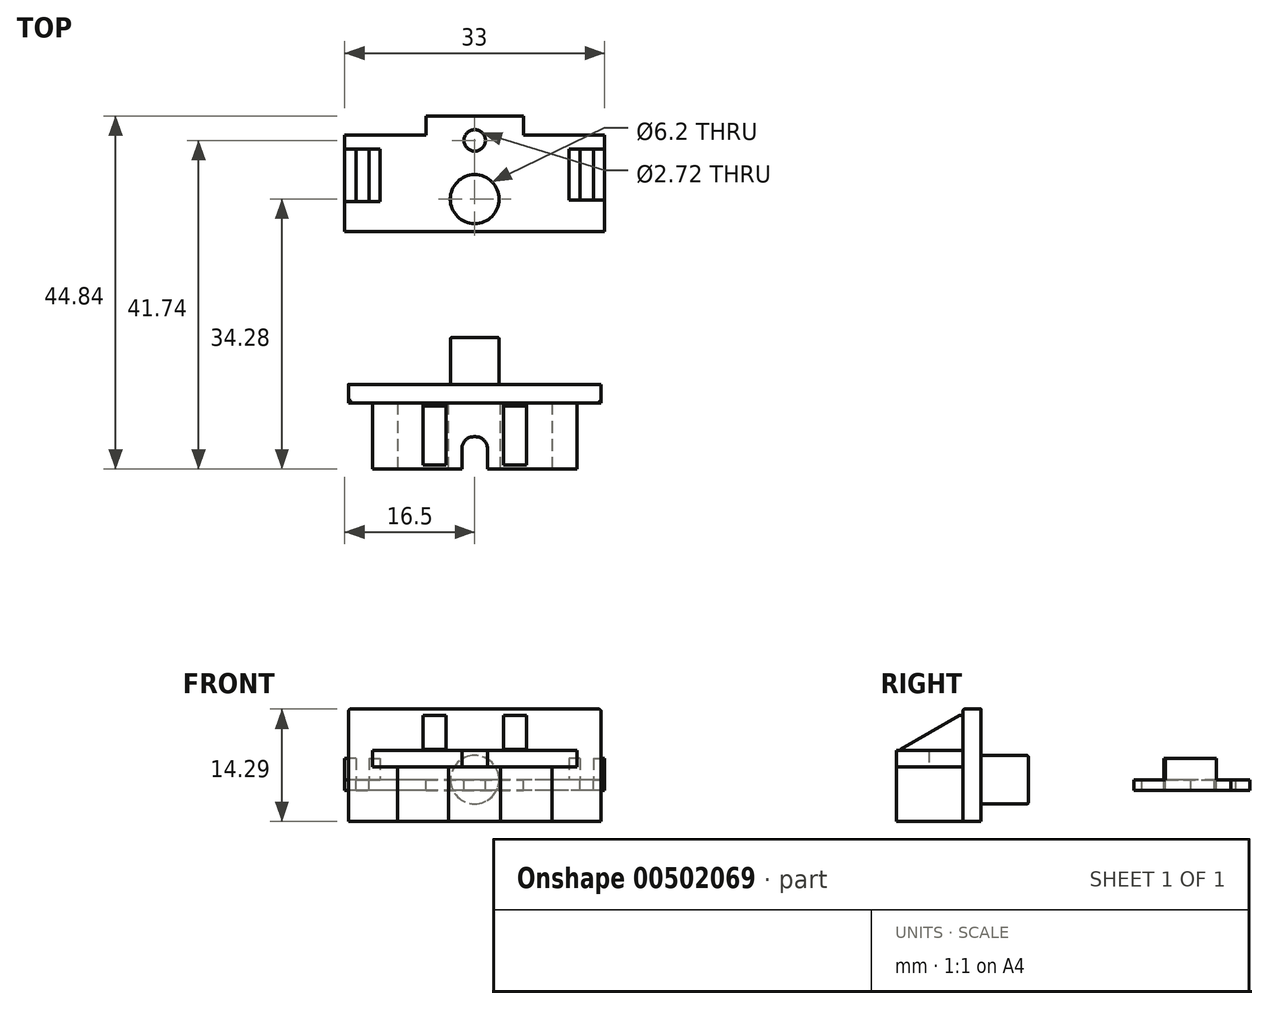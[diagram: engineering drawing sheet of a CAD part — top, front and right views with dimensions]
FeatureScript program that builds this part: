
annotation { "Feature Type Name" : "Feature", "Feature Type Description" : "" }
export const myFeature = defineFeature(function(context is Context, id is Id, definition is map)
    precondition{}
    {
        {
            var Q0;
            Q0=qCreatedBy(makeId("Top.planeOp"),FACE);
            var sketch = newSketch(context, id + "F0", { "sketchPlane" : qUnion([Q0])});
            skLineSegment(sketch, "E0.bottom", {"start": v(16.5, 6.15) * mm, "end": v(-16.5, 6.15) * mm});
            skLineSegment(sketch, "E0.top", {"start": v(16.5, -6.15) * mm, "end": v(-16.5, -6.15) * mm});
            skLineSegment(sketch, "E0.left", {"start": v(16.5, 6.15) * mm, "end": v(16.5, -6.15) * mm});
            skLineSegment(sketch, "E0.right", {"start": v(-16.5, 6.15) * mm, "end": v(-16.5, -6.15) * mm});
            skPoint(sketch, "E0.middle", {"position": v(0, 0) * mm});
            skCircle(sketch, "E1", {"center": v(0, -2) * mm, "radius": 3.1 * mm});
            skPoint(sketch, "E2.endSnap0", {"position": v(0, 6.15) * mm});
            skPoint(sketch, "E3", {"position": v(-6.2, 6.15) * mm});
            skPoint(sketch, "E4", {"position": v(6.2, 6.15) * mm});
            skLineSegment(sketch, "E5.bottom", {"start": v(-6.2, 6.15) * mm, "end": v(6.2, 6.15) * mm});
            skLineSegment(sketch, "E5.top", {"start": v(-6.2, 8.56) * mm, "end": v(6.2, 8.56) * mm});
            skLineSegment(sketch, "E5.left", {"start": v(-6.2, 6.15) * mm, "end": v(-6.2, 8.56) * mm});
            skLineSegment(sketch, "E5.right", {"start": v(6.2, 6.15) * mm, "end": v(6.2, 8.56) * mm});
            skCircle(sketch, "E6", {"center": v(0, 5.46) * mm, "radius": 1.36 * mm});
            skLineSegment(sketch, "E7", {"start": v(-15.1, 4.35) * mm, "end": v(-15.1, -2.31) * mm});
            skLineSegment(sketch, "E8", {"start": v(15.1, 4.35) * mm, "end": v(15.1, -2.15) * mm});
            skLineSegment(sketch, "E9", {"start": v(-13.4, -2.31) * mm, "end": v(-15.1, -2.31) * mm});
            skLineSegment(sketch, "E10", {"start": v(15.1, -2.15) * mm, "end": v(13.4, -2.15) * mm});
            skLineSegment(sketch, "E11", {"start": v(15.1, 4.35) * mm, "end": v(13.4, 4.35) * mm});
            skLineSegment(sketch, "E12", {"start": v(13.4, -2.15) * mm, "end": v(13.4, 4.35) * mm});
            skLineSegment(sketch, "E13", {"start": v(-13.4, 4.35) * mm, "end": v(-13.4, -2.3) * mm});
            skLineSegment(sketch, "E14", {"start": v(-15.1, 4.35) * mm, "end": v(-13.4, 4.35) * mm});
            skLineSegment(sketch, "E15", {"start": v(-15.1, 4.35) * mm, "end": v(-16.5, 4.35) * mm});
            skLineSegment(sketch, "E16", {"start": v(-15.1, -2.31) * mm, "end": v(-16.5, -2.31) * mm});
            skLineSegment(sketch, "E17.0", {"start": v(-12, 4.35) * mm, "end": v(-12, -2.3) * mm});
            skLineSegment(sketch, "E18", {"start": v(-13.4, 4.35) * mm, "end": v(-12, 4.35) * mm});
            skLineSegment(sketch, "E19", {"start": v(-13.4, -2.31) * mm, "end": v(-12, -2.3) * mm});
            skLineSegment(sketch, "E20", {"start": v(15.1, 4.35) * mm, "end": v(16.5, 4.35) * mm});
            skLineSegment(sketch, "E21", {"start": v(15.1, -2.15) * mm, "end": v(16.5, -2.15) * mm});
            skLineSegment(sketch, "E22.0", {"start": v(12, -2.15) * mm, "end": v(12, 4.35) * mm});
            skLineSegment(sketch, "E23", {"start": v(13.4, 4.35) * mm, "end": v(12, 4.35) * mm});
            skLineSegment(sketch, "E24", {"start": v(13.4, -2.15) * mm, "end": v(12, -2.15) * mm});
            skLineSegment(sketch, "E25.bottom", {"start": v(3.08, -25.55) * mm, "end": v(-3.07, -25.55) * mm});
            skLineSegment(sketch, "E25.top", {"start": v(3.08, -19.55) * mm, "end": v(-3.07, -19.55) * mm});
            skLineSegment(sketch, "E25.left", {"start": v(3.08, -25.55) * mm, "end": v(3.08, -19.55) * mm});
            skLineSegment(sketch, "E25.right", {"start": v(-3.07, -25.55) * mm, "end": v(-3.07, -19.55) * mm});
            skPoint(sketch, "E25.middle", {"position": v(0, -22.55) * mm});
            skLineSegment(sketch, "E26", {"start": v(0, -25.55) * mm, "end": v(16.03, -25.55) * mm});
            skLineSegment(sketch, "E27", {"start": v(0, -25.55) * mm, "end": v(-16.03, -25.55) * mm});
            skLineSegment(sketch, "E28.bottom", {"start": v(-16.03, -25.55) * mm, "end": v(16.03, -25.55) * mm});
            skLineSegment(sketch, "E28.top", {"start": v(-16.03, -27.88) * mm, "end": v(16.03, -27.88) * mm});
            skLineSegment(sketch, "E28.left", {"start": v(-16.03, -25.55) * mm, "end": v(-16.03, -27.88) * mm});
            skLineSegment(sketch, "E28.right", {"start": v(16.03, -25.55) * mm, "end": v(16.03, -27.88) * mm});
            skLineSegment(sketch, "E29.bottom", {"start": v(13, -27.88) * mm, "end": v(-13, -27.88) * mm});
            skLineSegment(sketch, "E29.top", {"start": v(13, -36.28) * mm, "end": v(-13, -36.28) * mm});
            skLineSegment(sketch, "E29.left", {"start": v(13, -27.88) * mm, "end": v(13, -36.28) * mm});
            skLineSegment(sketch, "E29.right", {"start": v(-13, -27.88) * mm, "end": v(-13, -36.28) * mm});
            skPoint(sketch, "E30", {"position": v(1.6, -36.28) * mm});
            skPoint(sketch, "E31", {"position": v(-1.61, -36.28) * mm});
            skPoint(sketch, "E32", {"position": v(0, -36.28) * mm});
            skLineSegment(sketch, "E33.bottom", {"start": v(-1.61, -36.28) * mm, "end": v(1.6, -36.28) * mm});
            skLineSegment(sketch, "E33.top", {"start": v(-1.61, -32.18) * mm, "end": v(1.6, -32.18) * mm});
            skLineSegment(sketch, "E33.left", {"start": v(-1.61, -36.28) * mm, "end": v(-1.61, -32.18) * mm});
            skLineSegment(sketch, "E33.right", {"start": v(1.6, -36.28) * mm, "end": v(1.6, -32.18) * mm});
            skLineSegment(sketch, "E34", {"start": v(-1.61, -32.18) * mm, "end": v(-3.31, -32.18) * mm});
            skLineSegment(sketch, "E35", {"start": v(1.6, -32.18) * mm, "end": v(3.3, -32.18) * mm});
            skLineSegment(sketch, "E36", {"start": v(-3.31, -36.28) * mm, "end": v(-3.31, -27.88) * mm});
            skLineSegment(sketch, "E37", {"start": v(3.3, -36.28) * mm, "end": v(3.3, -27.88) * mm});
            skLineSegment(sketch, "E38", {"start": v(-6.81, -27.88) * mm, "end": v(-6.8, -36.28) * mm});
            skLineSegment(sketch, "E39", {"start": v(6.8, -27.88) * mm, "end": v(6.81, -36.28) * mm});
            skLineSegment(sketch, "E40", {"start": v(-9.8, -27.88) * mm, "end": v(-9.8, -36.28) * mm});
            skLineSegment(sketch, "E41", {"start": v(9.8, -27.88) * mm, "end": v(9.8, -36.28) * mm});
            skLineSegment(sketch, "E42", {"start": v(0, -19.55) * mm, "end": v(0, -25.55) * mm});
            skSolve(sketch);
        }
        {
            var Q0;
            {var subQ10=sQuery(id+"F0.wireOp",EDGE,"E0.top");Q0=makeQuery(id+"F0.imprint","IMPRINT",FACE,{"disambiguationData":[TD([[makeQuery(id+"F0.imprint","IMPRINT",EDGE,{"derivedFrom":subQ10}),-1.0]])]});}
            var Q1;
            Q1=makeQuery(id+"F0.imprint","IMPRINT",FACE,{"disambiguationData":[TD([[makeQuery(id+"F0.imprint","IMPRINT",EDGE,{"derivedFrom":sQuery(id+"F0.wireOp",EDGE,"E7")}),-1.0]])]});
            var Q2;
            Q2=makeQuery(id+"F0.imprint","IMPRINT",FACE,{"disambiguationData":[TD([[makeQuery(id+"F0.imprint","IMPRINT",EDGE,{"derivedFrom":sQuery(id+"F0.wireOp",EDGE,"E12")}),1.0]])]});
            var Q3;
            Q3=makeQuery(id+"F0.imprint","IMPRINT",FACE,{"disambiguationData":[TD([[makeQuery(id+"F0.imprint","IMPRINT",EDGE,{"derivedFrom":sQuery(id+"F0.wireOp",EDGE,"E5.top")}),-1.0]])]});
            var Q4;
            Q4=makeQuery(id+"F0.imprint","IMPRINT",FACE,{"disambiguationData":[TD([[makeQuery(id+"F0.imprint","IMPRINT",EDGE,{"derivedFrom":sQuery(id+"F0.wireOp",EDGE,"E8")}),1.0]])]});
            var Q5;
            Q5=makeQuery(id+"F0.imprint","IMPRINT",FACE,{"disambiguationData":[TD([[makeQuery(id+"F0.imprint","IMPRINT",EDGE,{"derivedFrom":sQuery(id+"F0.wireOp",EDGE,"E13")}),1.0]])]});
            extrude(context, id + "F1", {"entities" : qUnion([Q0, Q1, Q2, Q3, Q4, Q5]), "oppositeDirection" : true, "depth" : 1.35 * mm});
        }
        {
            var Q0;
            Q0=makeQuery(id+"F0.imprint","IMPRINT",FACE,{"disambiguationData":[TD([[makeQuery(id+"F0.imprint","IMPRINT",EDGE,{"derivedFrom":sQuery(id+"F0.wireOp",EDGE,"E13")}),1.0]])]});
            var Q1;
            Q1=makeQuery(id+"F0.imprint","IMPRINT",FACE,{"disambiguationData":[TD([[makeQuery(id+"F0.imprint","IMPRINT",EDGE,{"derivedFrom":sQuery(id+"F0.wireOp",EDGE,"E12")}),1.0]])]});
            var Q2;
            Q2=makeQuery(id+"F0.imprint","IMPRINT",FACE,{"disambiguationData":[TD([[makeQuery(id+"F0.imprint","IMPRINT",EDGE,{"derivedFrom":sQuery(id+"F0.wireOp",EDGE,"E8")}),1.0]])]});
            var Q3;
            Q3=makeQuery(id+"F0.imprint","IMPRINT",FACE,{"disambiguationData":[TD([[makeQuery(id+"F0.imprint","IMPRINT",EDGE,{"derivedFrom":sQuery(id+"F0.wireOp",EDGE,"E7")}),-1.0]])]});
            extrude(context, id + "F2", {"entities" : qUnion([Q0, Q1, Q2, Q3]), "operationType" : NewBodyOperationType.ADD, "depth" : 2.73 * mm});
        }
        {
            var Q0;
            {var subQ0=sQuery(id+"F0.wireOp",EDGE,"E25.left");Q0=makeQuery(id+"F0.imprint","IMPRINT",FACE,{"disambiguationData":[TD([[makeQuery(id+"F0.imprint","IMPRINT",EDGE,{"derivedFrom":subQ0}),1.0]])]});}
            var Q1;
            Q1=sQuery(id+"F0.wireOp",EDGE,"E42");
            revolve(context, id + "F3", {"entities" : qUnion([Q0]), "axis" : qUnion([Q1]), "revolveType" : RevolveType.FULL});
        }
        {
            var Q0;
            {var subQ6=sQuery(id+"F0.wireOp",EDGE,"E28.left");Q0=makeQuery(id+"F0.imprint","IMPRINT",FACE,{"disambiguationData":[TD([[makeQuery(id+"F0.imprint","IMPRINT",EDGE,{"derivedFrom":subQ6}),1.0]])]});}
            extrude(context, id + "F4", {"entities" : qUnion([Q0]), "operationType" : NewBodyOperationType.ADD, "oppositeDirection" : true, "depth" : 5.3 * mm});
        }
        {
            var Q0;
            {var subQ6=sQuery(id+"F0.wireOp",EDGE,"E28.left");Q0=makeQuery(id+"F0.imprint","IMPRINT",FACE,{"disambiguationData":[TD([[makeQuery(id+"F0.imprint","IMPRINT",EDGE,{"derivedFrom":subQ6}),1.0]])]});}
            extrude(context, id + "F5", {"entities" : qUnion([Q0]), "operationType" : NewBodyOperationType.ADD, "depth" : 8.98 * mm});
        }
        {
            var Q0;
            {var subQ0=sQuery(id+"F0.wireOp",EDGE,"E29.left");Q0=makeQuery(id+"F0.imprint","IMPRINT",FACE,{"disambiguationData":[TD([[makeQuery(id+"F0.imprint","IMPRINT",EDGE,{"derivedFrom":subQ0}),-1.0]])]});}
            var Q1;
            {var subQ0=sQuery(id+"F0.wireOp",EDGE,"E39");Q1=makeQuery(id+"F0.imprint","IMPRINT",FACE,{"disambiguationData":[TD([[makeQuery(id+"F0.imprint","IMPRINT",EDGE,{"derivedFrom":subQ0}),1.0]])]});}
            var Q2;
            {var subQ6=sQuery(id+"F0.wireOp",EDGE,"E39");Q2=makeQuery(id+"F0.imprint","IMPRINT",FACE,{"disambiguationData":[TD([[makeQuery(id+"F0.imprint","IMPRINT",EDGE,{"derivedFrom":subQ6}),-1.0]])]});}
            var Q3;
            Q3=makeQuery(id+"F0.imprint","IMPRINT",FACE,{"disambiguationData":[TD([[makeQuery(id+"F0.imprint","IMPRINT",EDGE,{"derivedFrom":sQuery(id+"F0.wireOp",EDGE,"E33.top")}),1.0]])]});
            var Q4;
            {var subQ0=sQuery(id+"F0.wireOp",EDGE,"E33.right");Q4=makeQuery(id+"F0.imprint","IMPRINT",FACE,{"disambiguationData":[TD([[makeQuery(id+"F0.imprint","IMPRINT",EDGE,{"derivedFrom":subQ0}),-1.0]])]});}
            var Q5;
            {var subQ0=sQuery(id+"F0.wireOp",EDGE,"E33.left");Q5=makeQuery(id+"F0.imprint","IMPRINT",FACE,{"disambiguationData":[TD([[makeQuery(id+"F0.imprint","IMPRINT",EDGE,{"derivedFrom":subQ0}),1.0]])]});}
            var Q6;
            {var subQ4=sQuery(id+"F0.wireOp",EDGE,"E38");Q6=makeQuery(id+"F0.imprint","IMPRINT",FACE,{"disambiguationData":[TD([[makeQuery(id+"F0.imprint","IMPRINT",EDGE,{"derivedFrom":subQ4}),1.0]])]});}
            var Q7;
            {var subQ0=sQuery(id+"F0.wireOp",EDGE,"E38");Q7=makeQuery(id+"F0.imprint","IMPRINT",FACE,{"disambiguationData":[TD([[makeQuery(id+"F0.imprint","IMPRINT",EDGE,{"derivedFrom":subQ0}),-1.0]])]});}
            var Q8;
            {var subQ0=sQuery(id+"F0.wireOp",EDGE,"E29.right");Q8=makeQuery(id+"F0.imprint","IMPRINT",FACE,{"disambiguationData":[TD([[makeQuery(id+"F0.imprint","IMPRINT",EDGE,{"derivedFrom":subQ0}),1.0]])]});}
            extrude(context, id + "F6", {"entities" : qUnion([Q0, Q1, Q2, Q3, Q4, Q5, Q6, Q7, Q8]), "depth" : 2.1 * mm});
        }
        {
            var Q0;
            Q0=makeQuery(id+"F6.opExtrude","SWEPT_EDGE",EDGE,{"disambiguationData":[OSD([sQuery(id+"F0.wireOp",EDGE,"E33.top"),sQuery(id+"F0.wireOp",EDGE,"E33.right"),sQuery(id+"F0.wireOp",EDGE,"E35")])]});
            var Q1;
            Q1=makeQuery(id+"F6.opExtrude","SWEPT_EDGE",EDGE,{"disambiguationData":[OSD([sQuery(id+"F0.wireOp",EDGE,"E33.top"),sQuery(id+"F0.wireOp",EDGE,"E33.left"),sQuery(id+"F0.wireOp",EDGE,"E34")])]});
            fillet(context, id + "F7", {"entities" : qUnion([Q0, Q1]), "radius" : 1.5 * mm, "tangentPropagation" : true, "allowEdgeOverflow" : false});
        }
        {
            var Q0;
            {var subQ0=sQuery(id+"F0.wireOp",EDGE,"E38");Q0=makeQuery(id+"F0.imprint","IMPRINT",FACE,{"disambiguationData":[TD([[makeQuery(id+"F0.imprint","IMPRINT",EDGE,{"derivedFrom":subQ0}),-1.0]])]});}
            var Q1;
            {var subQ4=sQuery(id+"F0.wireOp",EDGE,"E38");Q1=makeQuery(id+"F0.imprint","IMPRINT",FACE,{"disambiguationData":[TD([[makeQuery(id+"F0.imprint","IMPRINT",EDGE,{"derivedFrom":subQ4}),1.0]])]});}
            var Q2;
            {var subQ6=sQuery(id+"F0.wireOp",EDGE,"E39");Q2=makeQuery(id+"F0.imprint","IMPRINT",FACE,{"disambiguationData":[TD([[makeQuery(id+"F0.imprint","IMPRINT",EDGE,{"derivedFrom":subQ6}),-1.0]])]});}
            var Q3;
            {var subQ0=sQuery(id+"F0.wireOp",EDGE,"E39");Q3=makeQuery(id+"F0.imprint","IMPRINT",FACE,{"disambiguationData":[TD([[makeQuery(id+"F0.imprint","IMPRINT",EDGE,{"derivedFrom":subQ0}),1.0]])]});}
            extrude(context, id + "F8", {"entities" : qUnion([Q0, Q1, Q2, Q3]), "oppositeDirection" : true, "depth" : 6.94 * mm});
        }
        {
            var Q0;
            Q0=makeQuery(id+"F6.opExtrude","SWEPT_BODY",BODY,{"disambiguationData":[OSD([sQuery(id+"F0.wireOp",EDGE,"E29.bottom"),sQuery(id+"F0.wireOp",EDGE,"E29.top"),sQuery(id+"F0.wireOp",EDGE,"E29.left"),sQuery(id+"F0.wireOp",EDGE,"E29.right"),sQuery(id+"F0.wireOp",EDGE,"E33.top"),sQuery(id+"F0.wireOp",EDGE,"E33.left"),sQuery(id+"F0.wireOp",EDGE,"E33.right")])]});
            var Q1;
            Q1=makeQuery(id+"F8.opExtrude","SWEPT_BODY",BODY,{"disambiguationData":[OSD([sQuery(id+"F0.wireOp",EDGE,"E29.bottom"),sQuery(id+"F0.wireOp",EDGE,"E29.top"),sQuery(id+"F0.wireOp",EDGE,"E36"),sQuery(id+"F0.wireOp",EDGE,"E40")])]});
            var Q2;
            Q2=makeQuery(id+"F8.opExtrude","SWEPT_BODY",BODY,{"disambiguationData":[OSD([sQuery(id+"F0.wireOp",EDGE,"E29.bottom"),sQuery(id+"F0.wireOp",EDGE,"E29.top"),sQuery(id+"F0.wireOp",EDGE,"E37"),sQuery(id+"F0.wireOp",EDGE,"E41")])]});
            var Q3;
            {var subQ0=sQuery(id+"F0.wireOp",EDGE,"E28.left");var subQ1=sQuery(id+"F0.wireOp",EDGE,"E28.top");Q3=makeQuery(id+"F5.boolean.opBoolean","MERGE",EDGE,{"derivedFrom":[makeQuery(id+"F4.opExtrude","SWEPT_EDGE",EDGE,{"disambiguationData":[OSD([subQ1,subQ0])]}),makeQuery(id+"F5.opExtrude","SWEPT_EDGE",EDGE,{"disambiguationData":[OSD([subQ1,subQ0])]})]});}
            transform(context, id + "F9", {"entities" : qUnion([Q0, Q1, Q2]), "transformType" : TransformType.TRANSLATION_3D, "dx" : 0 * mm, "dy" : 0 * mm, "dz" : 1.63 * mm, "makeCopy" : false});
        }
        {
            var Q0;
            {var subQ0=sQuery(id+"F0.wireOp",EDGE,"E29.bottom");var subQ1=sQuery(id+"F0.wireOp",EDGE,"E28.top");Q0=makeQuery(id+"F5.boolean.opBoolean","MERGE",FACE,{"derivedFrom":[makeQuery(id+"F4.opExtrude","SWEPT_FACE",FACE,{"disambiguationData":[OSD([subQ1,subQ0])]}),makeQuery(id+"F5.opExtrude","SWEPT_FACE",FACE,{"disambiguationData":[OSD([subQ1,subQ0])]})]});}
            var sketch = newSketch(context, id + "F10", { "sketchPlane" : qUnion([Q0])});
            skLineSegment(sketch, "E43", {"start": v(-12.78, -5.3) * mm, "end": v(-12.78, 1.64) * mm});
            skLineSegment(sketch, "E44.bottom", {"start": v(-3.64, 3.73) * mm, "end": v(-6.57, 3.73) * mm});
            skLineSegment(sketch, "E44.top", {"start": v(-3.64, 8.16) * mm, "end": v(-6.57, 8.16) * mm});
            skLineSegment(sketch, "E44.left", {"start": v(-3.64, 3.73) * mm, "end": v(-3.64, 8.16) * mm});
            skLineSegment(sketch, "E44.right", {"start": v(-6.57, 3.73) * mm, "end": v(-6.57, 8.16) * mm});
            skSolve(sketch);
        }
        {
            var Q0;
            Q0=makeQuery(id+"F10.imprint","IMPRINT",FACE,{"disambiguationData":[TD([[makeQuery(id+"F10.imprint","IMPRINT",EDGE,{"derivedFrom":sQuery(id+"F10.wireOp",EDGE,"E44.bottom")}),-1.0]])]});
            extrude(context, id + "F11", {"entities" : qUnion([Q0]), "depth" : 7.9 * mm});
        }
        {
            var Q0;
            Q0=makeQuery(id+"F11.opExtrude","CAP_EDGE",EDGE,{"disambiguationData":[OSD([sQuery(id+"F10.wireOp",EDGE,"E44.top")])],"isStart":false});
            chamfer(context, id + "F12", {"entities" : qUnion([Q0]), "chamferType" : ChamferType.TWO_OFFSETS, "width1" : 4.3 * mm, "oppositeDirection" : false, "width2" : 7.5 * mm, "tangentPropagation" : true});
        }
        {
            var Q0;
            Q0=makeQuery(id+"F11.opExtrude","SWEPT_BODY",BODY,{"disambiguationData":[OSD([sQuery(id+"F10.wireOp",EDGE,"E44.bottom"),sQuery(id+"F10.wireOp",EDGE,"E44.top"),sQuery(id+"F10.wireOp",EDGE,"E44.left"),sQuery(id+"F10.wireOp",EDGE,"E44.right")])]});
            var Q1;
            Q1=qCreatedBy(makeId("Right.planeOp"),FACE);
            mirror(context, id + "F13", {"entities" : qUnion([Q0]), "mirrorPlane" : qUnion([Q1])});
        }
        {
            var Q0;
            Q0=makeQuery(id+"F5.opExtrude","CAP_EDGE",EDGE,{"disambiguationData":[OSD([sQuery(id+"F0.wireOp",EDGE,"E28.left")])],"isStart":false});
            var Q1;
            Q1=makeQuery(id+"F5.opExtrude","CAP_EDGE",EDGE,{"disambiguationData":[OSD([sQuery(id+"F0.wireOp",EDGE,"E28.right")])],"isStart":false});
            var Q2;
            Q2=makeQuery(id+"F5.opExtrude","CAP_EDGE",EDGE,{"disambiguationData":[OSD([sQuery(id+"F0.wireOp",EDGE,"E28.top"),sQuery(id+"F0.wireOp",EDGE,"E29.bottom")])],"isStart":false});
            var Q3;
            Q3=makeQuery(id+"F5.opExtrude","CAP_EDGE",EDGE,{"disambiguationData":[OSD([sQuery(id+"F0.wireOp",EDGE,"E28.bottom")])],"isStart":false});
            fillet(context, id + "F14", {"entities" : qUnion([Q0, Q1, Q2, Q3]), "radius" : 0.3 * mm, "tangentPropagation" : true, "allowEdgeOverflow" : false});
        }
        {
            var Q0;
            Q0=makeQuery(id+"F3.opRevolve","SWEPT_EDGE",EDGE,{"disambiguationData":[OSD([sQuery(id+"F0.wireOp",EDGE,"E25.top"),sQuery(id+"F0.wireOp",EDGE,"E25.left")])]});
            fillet(context, id + "F15", {"entities" : qUnion([Q0]), "radius" : 0.2 * mm, "tangentPropagation" : true, "allowEdgeOverflow" : false});
        }
    });
